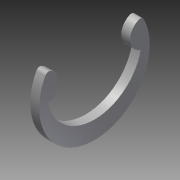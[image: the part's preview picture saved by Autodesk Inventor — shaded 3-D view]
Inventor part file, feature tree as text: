
AUTODESK INVENTOR PART (.ipt)
format: ipt  version: 2013 (Build 170138000, 138)  size: 88,064 bytes
history: native  units: in
note: dims shown in document units (in); Inventor stores cm internally (conversion verified against a paired STEP export)
features: extrude x1, other x1, imported_body x1
ambient origin geometry x8: Origin, YZ Plane, XZ Plane, XY Plane, X Axis, Y Axis, Z Axis, Center Point
feature tree (3):
  extrude  "Extrude1"  [1 undecoded]
  other  "217-2428-027 Rev1_97414A6301"
  imported_body  "Base1"
note: 1 required parameter value undecoded (feature->parameter linkage not recoverable at this tier; creation-order binding heuristic only, values carry confidence <= 0.55)
